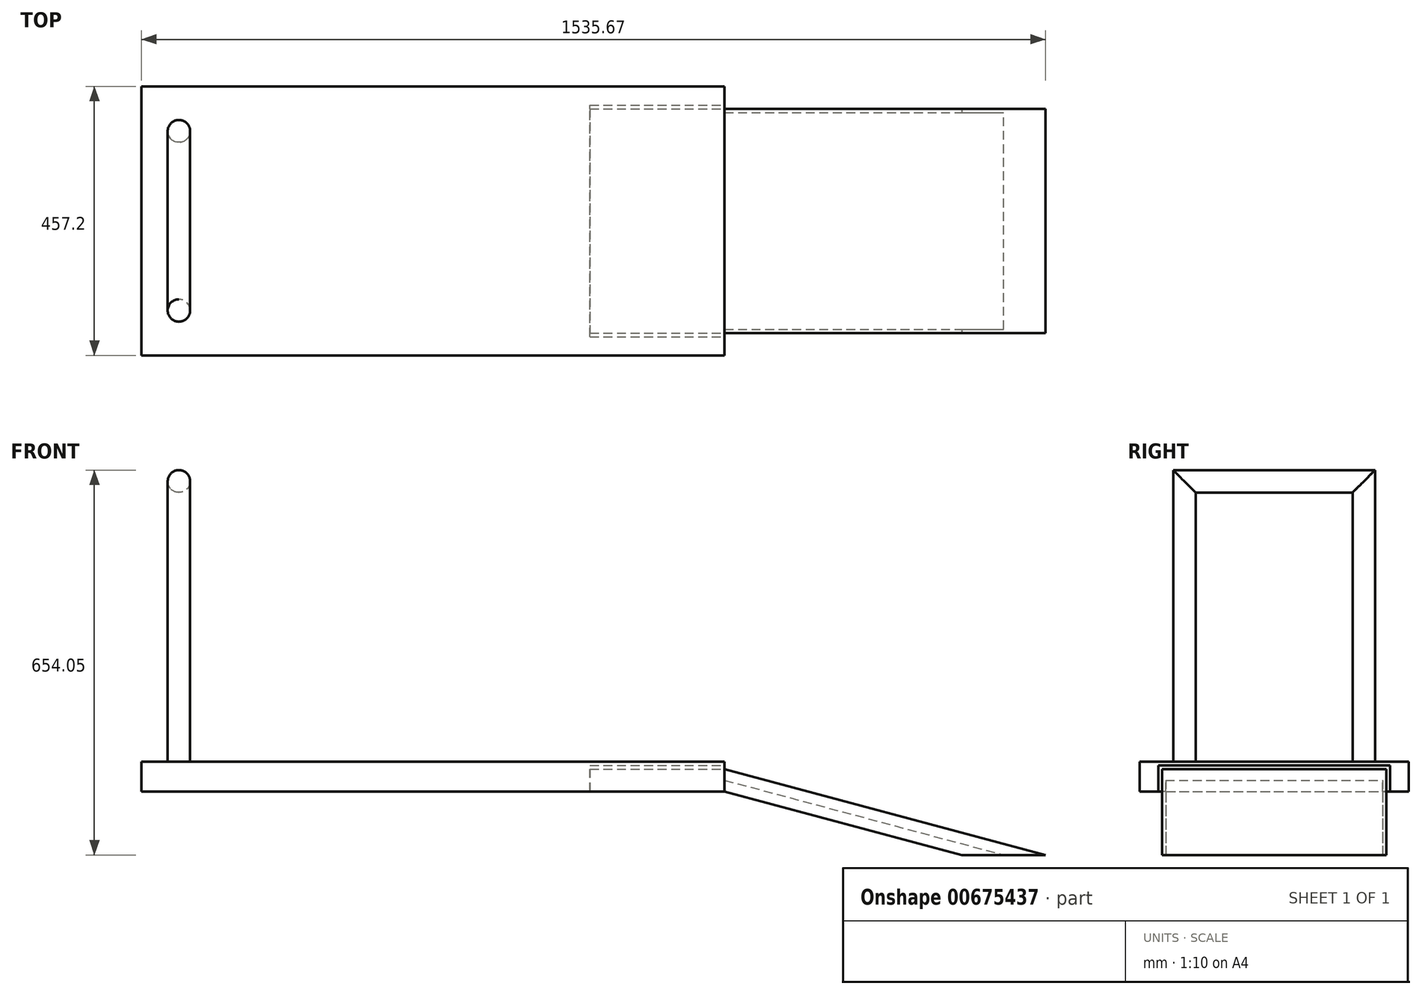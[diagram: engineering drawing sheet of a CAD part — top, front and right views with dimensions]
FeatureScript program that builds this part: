
annotation { "Feature Type Name" : "Feature", "Feature Type Description" : "" }
export const myFeature = defineFeature(function(context is Context, id is Id, definition is map)
    precondition{}
    {
        {
            var Q0;
            Q0=qCreatedBy(makeId("Top.planeOp"),FACE);
            var sketch = newSketch(context, id + "F0", { "sketchPlane" : qUnion([Q0])});
            skLineSegment(sketch, "E0.bottom", {"start": v(0, 0) * mm, "end": v(990.6, 0) * mm});
            skLineSegment(sketch, "E0.top", {"start": v(0, 457.2) * mm, "end": v(990.6, 457.2) * mm});
            skLineSegment(sketch, "E0.left", {"start": v(0, 0) * mm, "end": v(0, 457.2) * mm});
            skLineSegment(sketch, "E0.right", {"start": v(990.6, 0) * mm, "end": v(990.6, 457.2) * mm});
            skSolve(sketch);
        }
        {
            var Q0;
            Q0 = qSketchRegion(id + "F0", true);
            extrude(context, id + "F1", {"entities" : qUnion([Q0]), "depth" : 25.4 * mm, "offsetDistance" : 25.4 * mm, "hasSecondDirection" : true, "secondDirectionOppositeDirection" : true, "secondDirectionDepth" : 25.4 * mm});
        }
        {
            var Q0;
            Q0=makeQuery(id+"F1.opExtrude","CAP_FACE",FACE,{"disambiguationData":[OSD([sQuery(id+"F0.wireOp",EDGE,"E0.bottom"),sQuery(id+"F0.wireOp",EDGE,"E0.top"),sQuery(id+"F0.wireOp",EDGE,"E0.left"),sQuery(id+"F0.wireOp",EDGE,"E0.right")])],"isStart":false});
            var sketch = newSketch(context, id + "F2", { "sketchPlane" : qUnion([Q0])});
            skPoint(sketch, "E1", {"position": v(0, 228.6) * mm});
            skPoint(sketch, "E2", {"position": v(0, 381) * mm});
            skPoint(sketch, "E3", {"position": v(0, 76.2) * mm});
            skPoint(sketch, "E4", {"position": v(63.5, 381) * mm});
            skPoint(sketch, "E5", {"position": v(63.5, 76.2) * mm});
            skLineSegment(sketch, "E6.bottom", {"start": v(82.55, 400.05) * mm, "end": v(44.45, 400.05) * mm});
            skLineSegment(sketch, "E6.top", {"start": v(82.55, 361.95) * mm, "end": v(44.45, 361.95) * mm});
            skLineSegment(sketch, "E6.left", {"start": v(82.55, 400.05) * mm, "end": v(82.55, 361.95) * mm});
            skLineSegment(sketch, "E6.right", {"start": v(44.45, 400.05) * mm, "end": v(44.45, 361.95) * mm});
            skLineSegment(sketch, "E7.bottom", {"start": v(82.55, 95.25) * mm, "end": v(44.45, 95.25) * mm});
            skLineSegment(sketch, "E7.top", {"start": v(82.55, 57.15) * mm, "end": v(44.45, 57.15) * mm});
            skLineSegment(sketch, "E7.left", {"start": v(82.55, 95.25) * mm, "end": v(82.55, 57.15) * mm});
            skLineSegment(sketch, "E7.right", {"start": v(44.45, 95.25) * mm, "end": v(44.45, 57.15) * mm});
            skSolve(sketch);
        }
        {
            var Q0;
            Q0 = qSketchRegion(id + "F2", true);
            extrude(context, id + "F3", {"entities" : qUnion([Q0]), "operationType" : NewBodyOperationType.ADD, "depth" : 457.2 * mm, "offsetDistance" : 25.4 * mm});
        }
        {
            var Q0;
            Q0=makeQuery(id+"F3.opExtrude","SWEPT_FACE",FACE,{"disambiguationData":[OSD([sQuery(id+"F2.wireOp",EDGE,"E7.right")])]});
            var sketch = newSketch(context, id + "F4", { "sketchPlane" : qUnion([Q0])});
            skLineSegment(sketch, "E8.bottom", {"start": v(-57.15, 482.6) * mm, "end": v(-400.05, 482.6) * mm});
            skLineSegment(sketch, "E8.top", {"start": v(-57.15, 520.7) * mm, "end": v(-400.05, 520.7) * mm});
            skLineSegment(sketch, "E8.left", {"start": v(-57.15, 482.6) * mm, "end": v(-57.15, 520.7) * mm});
            skLineSegment(sketch, "E8.right", {"start": v(-400.05, 482.6) * mm, "end": v(-400.05, 520.7) * mm});
            skSolve(sketch);
        }
        {
            var Q0;
            Q0 = qSketchRegion(id + "F4", true);
            extrude(context, id + "F5", {"entities" : qUnion([Q0]), "operationType" : NewBodyOperationType.ADD, "oppositeDirection" : true, "depth" : 38.1 * mm, "offsetDistance" : 25.4 * mm});
        }
        {
            var Q0;
            Q0=makeQuery(id+"F5.opExtrude","CAP_EDGE",EDGE,{"disambiguationData":[OSD([sQuery(id+"F4.wireOp",EDGE,"E8.top")])],"isStart":false});
            var Q1;
            Q1=makeQuery(id+"F5.opExtrude","CAP_EDGE",EDGE,{"disambiguationData":[OSD([sQuery(id+"F4.wireOp",EDGE,"E8.bottom")])],"isStart":false});
            var Q2;
            Q2=makeQuery(id+"F3.opExtrude","SWEPT_EDGE",EDGE,{"disambiguationData":[OSD([sQuery(id+"F2.wireOp",EDGE,"E6.top"),sQuery(id+"F2.wireOp",EDGE,"E6.left")])]});
            var Q3;
            Q3=makeQuery(id+"F3.opExtrude","SWEPT_EDGE",EDGE,{"disambiguationData":[OSD([sQuery(id+"F2.wireOp",EDGE,"E6.top"),sQuery(id+"F2.wireOp",EDGE,"E6.right")])]});
            var Q4;
            Q4=makeQuery(id+"F5.boolean.opBoolean","MERGE",EDGE,{"derivedFrom":[makeQuery(id+"F3.opExtrude","SWEPT_EDGE",EDGE,{"disambiguationData":[OSD([sQuery(id+"F2.wireOp",EDGE,"E6.bottom"),sQuery(id+"F2.wireOp",EDGE,"E6.left")])]}),makeQuery(id+"F5.opExtrude","CAP_EDGE",EDGE,{"disambiguationData":[OSD([sQuery(id+"F4.wireOp",EDGE,"E8.right")])],"isStart":false})]});
            var Q5;
            Q5=makeQuery(id+"F5.boolean.opBoolean","MERGE",EDGE,{"derivedFrom":[makeQuery(id+"F3.opExtrude","SWEPT_EDGE",EDGE,{"disambiguationData":[OSD([sQuery(id+"F2.wireOp",EDGE,"E7.top"),sQuery(id+"F2.wireOp",EDGE,"E7.left")])]}),makeQuery(id+"F5.opExtrude","CAP_EDGE",EDGE,{"disambiguationData":[OSD([sQuery(id+"F4.wireOp",EDGE,"E8.left")])],"isStart":false})]});
            var Q6;
            Q6=makeQuery(id+"F5.boolean.opBoolean","MERGE",EDGE,{"derivedFrom":[makeQuery(id+"F3.opExtrude","SWEPT_EDGE",EDGE,{"disambiguationData":[OSD([sQuery(id+"F2.wireOp",EDGE,"E7.top"),sQuery(id+"F2.wireOp",EDGE,"E7.right")])]}),makeQuery(id+"F5.opExtrude","CAP_EDGE",EDGE,{"disambiguationData":[OSD([sQuery(id+"F4.wireOp",EDGE,"E8.left")])],"isStart":true})]});
            var Q7;
            Q7=makeQuery(id+"F5.opExtrude","CAP_EDGE",EDGE,{"disambiguationData":[OSD([sQuery(id+"F4.wireOp",EDGE,"E8.top")])],"isStart":true});
            var Q8;
            Q8=makeQuery(id+"F5.boolean.opBoolean","MERGE",EDGE,{"derivedFrom":[makeQuery(id+"F3.opExtrude","SWEPT_EDGE",EDGE,{"disambiguationData":[OSD([sQuery(id+"F2.wireOp",EDGE,"E6.bottom"),sQuery(id+"F2.wireOp",EDGE,"E6.right")])]}),makeQuery(id+"F5.opExtrude","CAP_EDGE",EDGE,{"disambiguationData":[OSD([sQuery(id+"F4.wireOp",EDGE,"E8.right")])],"isStart":true})]});
            var Q9;
            Q9=makeQuery(id+"F3.opExtrude","SWEPT_EDGE",EDGE,{"disambiguationData":[OSD([sQuery(id+"F2.wireOp",EDGE,"E7.bottom"),sQuery(id+"F2.wireOp",EDGE,"E7.right")])]});
            var Q10;
            Q10=makeQuery(id+"F3.opExtrude","SWEPT_EDGE",EDGE,{"disambiguationData":[OSD([sQuery(id+"F2.wireOp",EDGE,"E7.bottom"),sQuery(id+"F2.wireOp",EDGE,"E7.left")])]});
            var Q11;
            Q11=makeQuery(id+"F5.opExtrude","CAP_EDGE",EDGE,{"disambiguationData":[OSD([sQuery(id+"F4.wireOp",EDGE,"E8.bottom")])],"isStart":true});
            fillet(context, id + "F6", {"entities" : qUnion([Q0, Q1, Q2, Q3, Q4, Q5, Q6, Q7, Q8, Q9, Q10, Q11]), "radius" : 19.05 * mm, "tangentPropagation" : true, "allowEdgeOverflow" : false});
        }
        {
            var Q0;
            Q0=makeQuery(id+"F1.opExtrude","SWEPT_FACE",FACE,{"disambiguationData":[OSD([sQuery(id+"F0.wireOp",EDGE,"E0.bottom")])]});
            var sketch = newSketch(context, id + "F7", { "sketchPlane" : qUnion([Q0])});
            skPoint(sketch, "E9", {"position": v(990.6, 12.7) * mm});
            skPoint(sketch, "E10", {"position": v(990.6, -25.4) * mm});
            skPoint(sketch, "E11", {"position": v(1393.47, -133.35) * mm});
            skPoint(sketch, "E12", {"position": v(1535.67, -133.35) * mm});
            skLineSegment(sketch, "E13", {"start": v(1393.47, -133.35) * mm, "end": v(1535.67, -133.35) * mm});
            skLineSegment(sketch, "E14", {"start": v(1535.67, -133.35) * mm, "end": v(990.6, 12.7) * mm});
            skLineSegment(sketch, "E15", {"start": v(990.6, -25.4) * mm, "end": v(990.6, 12.7) * mm});
            skLineSegment(sketch, "E16", {"start": v(990.6, -25.4) * mm, "end": v(1393.47, -133.35) * mm});
            skSolve(sketch);
        }
        {
            var Q0;
            Q0 = qSketchRegion(id + "F7", true);
            extrude(context, id + "F8", {"entities" : qUnion([Q0]), "operationType" : NewBodyOperationType.ADD, "oppositeDirection" : true, "depth" : 419.1 * mm, "offsetDistance" : 25.4 * mm, "hasSecondDirection" : true, "secondDirectionOppositeDirection" : true, "secondDirectionDepth" : 38.1 * mm});
        }
        {
            var Q0;
            Q0=makeQuery(id+"F1.opExtrude","SWEPT_FACE",FACE,{"disambiguationData":[OSD([sQuery(id+"F0.wireOp",EDGE,"E0.right")])]});
            var sketch = newSketch(context, id + "F9", { "sketchPlane" : qUnion([Q0])});
            skPoint(sketch, "E17", {"position": v(425.45, -25.4) * mm});
            skPoint(sketch, "E18", {"position": v(31.75, -25.4) * mm});
            skPoint(sketch, "E19", {"position": v(31.75, 19.05) * mm});
            skPoint(sketch, "E20", {"position": v(425.45, 19.05) * mm});
            skLineSegment(sketch, "E21", {"start": v(31.75, 19.05) * mm, "end": v(425.45, 19.05) * mm});
            skLineSegment(sketch, "E22", {"start": v(425.45, -25.4) * mm, "end": v(425.45, 19.05) * mm});
            skLineSegment(sketch, "E23", {"start": v(419.1, -25.4) * mm, "end": v(425.45, -25.4) * mm});
            skLineSegment(sketch, "E24", {"start": v(419.1, 12.7) * mm, "end": v(419.1, -25.4) * mm});
            skLineSegment(sketch, "E25", {"start": v(419.1, 12.7) * mm, "end": v(38.1, 12.7) * mm});
            skLineSegment(sketch, "E26", {"start": v(31.75, -25.4) * mm, "end": v(38.1, -25.4) * mm});
            skLineSegment(sketch, "E27", {"start": v(38.1, 12.7) * mm, "end": v(38.1, -25.4) * mm});
            skLineSegment(sketch, "E28", {"start": v(31.75, -25.4) * mm, "end": v(31.75, 19.05) * mm});
            skSolve(sketch);
        }
        {
            var Q0;
            Q0 = qSketchRegion(id + "F9", true);
            extrude(context, id + "F10", {"entities" : qUnion([Q0]), "operationType" : NewBodyOperationType.REMOVE, "oppositeDirection" : true, "depth" : 228.6 * mm, "offsetDistance" : 25.4 * mm});
        }
        {
            var Q0;
            Q0=makeQuery(id+"F10.boolean.opBoolean","MERGE",FACE,{"derivedFrom":[makeQuery(id+"F8.opExtrude","CAP_FACE",FACE,{"disambiguationData":[OSD([sQuery(id+"F7.wireOp",EDGE,"E13"),sQuery(id+"F7.wireOp",EDGE,"E14"),sQuery(id+"F7.wireOp",EDGE,"E15"),sQuery(id+"F7.wireOp",EDGE,"E16")])],"isStart":false}),makeQuery(id+"F10.opExtrude","SWEPT_FACE",FACE,{"disambiguationData":[OSD([sQuery(id+"F9.wireOp",EDGE,"E24")])]})]});
            var sketch = newSketch(context, id + "F11", { "sketchPlane" : qUnion([Q0])});
            skPoint(sketch, "E29", {"position": v(-1464.57, -133.35) * mm});
            skPoint(sketch, "E30", {"position": v(-990.6, -6.35) * mm});
            skLineSegment(sketch, "E31", {"start": v(-1464.57, -133.35) * mm, "end": v(-1393.47, -133.35) * mm});
            skLineSegment(sketch, "E32", {"start": v(-990.6, -25.4) * mm, "end": v(-990.6, -6.35) * mm});
            skLineSegment(sketch, "E33", {"start": v(-990.6, -6.35) * mm, "end": v(-1464.57, -133.35) * mm});
            skLineSegment(sketch, "E34", {"start": v(-1393.47, -133.35) * mm, "end": v(-990.6, -25.4) * mm});
            skSolve(sketch);
        }
        {
            var Q0;
            Q0 = qSketchRegion(id + "F11", true);
            extrude(context, id + "F12", {"entities" : qUnion([Q0]), "operationType" : NewBodyOperationType.REMOVE, "oppositeDirection" : true, "depth" : 374.65 * mm, "offsetDistance" : 25.4 * mm, "hasSecondDirection" : true, "secondDirectionOppositeDirection" : true, "secondDirectionDepth" : 6.35 * mm});
        }
    });
